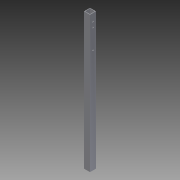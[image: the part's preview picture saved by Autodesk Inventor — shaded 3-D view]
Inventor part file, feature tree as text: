
AUTODESK INVENTOR PART (.ipt)
format: ipt  version: 2013 (Build 170138000, 138)  size: 107,520 bytes
history: native  units: in
note: dims shown in document units (in); Inventor stores cm internally (conversion verified against a paired STEP export)
features: reference x7, sketch x3, other x2, extrude x1
ambient origin geometry x8: Origin, YZ Plane, XZ Plane, XY Plane, X Axis, Y Axis, Z Axis, Center Point
bodies: Solid1 (feature_tree)
feature tree (13):
  extrude  "Extrusion1"  Depth=1.0in
  sketch  "Sketch1"  dims[d0=1.0in d2=1.0in]
  sketch  "Sketch5"  dims[d3=0.0625in]
  reference  "Reference10"
  reference  "Reference11"
  reference  "Reference12"
  sketch  "Sketch6"  dims[d4=23.375in d5=0.0in d10=100.0in d11=0.0in d12=100.0in d13=0.0in]
  reference  "Reference13"
  reference  "Reference14"
  reference  "Reference15"
  reference  "Reference16"
  other  "Cut3"
  other  "Cut4"
